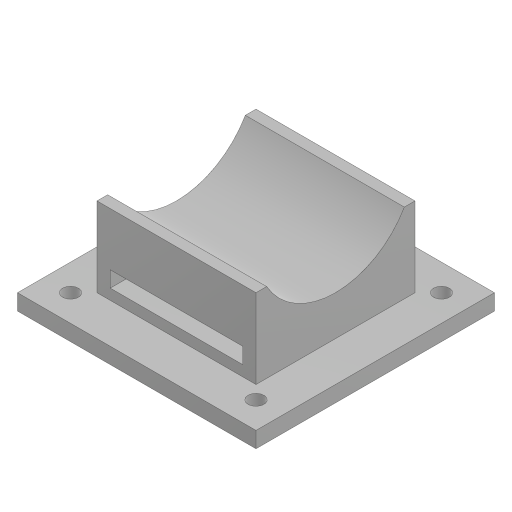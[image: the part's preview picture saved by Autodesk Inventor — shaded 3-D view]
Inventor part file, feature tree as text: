
AUTODESK INVENTOR PART (.ipt)
format: ipt  version: 2023.1 (Build 271208000, 208)  size: 153,088 bytes
history: native  units: mm
features: extrude x5, sketch x5
ambient origin geometry x8: Origin, YZ Plane, XZ Plane, XY Plane, X Axis, Y Axis, Z Axis, Center Point
bodies: Volumenkörper1 (feature_tree)
feature tree (10):
  extrude  "Extrusion1"  Depth=5.0mm
  extrude  "Extrusion2"  Depth=3.0mm
  extrude  "Extrusion3"  Depth=30.0mm
  extrude  "Extrusion4"  Depth=30.0mm
  extrude  "Extrusion5"  TaperAngle=0.0deg  [1 undecoded]
  sketch  "Skizze1"  dims[d0=45.0mm d1=5.0mm]
  sketch  "Skizze2"  dims[d2=35.0mm d3=3.0mm]
  sketch  "Skizze3"  dims[d5=3.0mm d6=0.0mm d7=30.0mm]
  sketch  "Skizze4"  dims[d8=30.0mm d9=0.0mm d10=30.0mm]
  sketch  "Skizze5"  dims[d11=0.0mm d12=0.0mm d15=0.0mm d16=0.0mm d18=7.5mm d19=25.0mm d20=3.0mm d21=2.0mm d22=0.0mm d23=0.0mm d24=15.0mm d13=0.5mm d14=0.872665mm]
note: 1 required parameter value undecoded (feature->parameter linkage not recoverable at this tier; creation-order binding heuristic only, values carry confidence <= 0.55)
